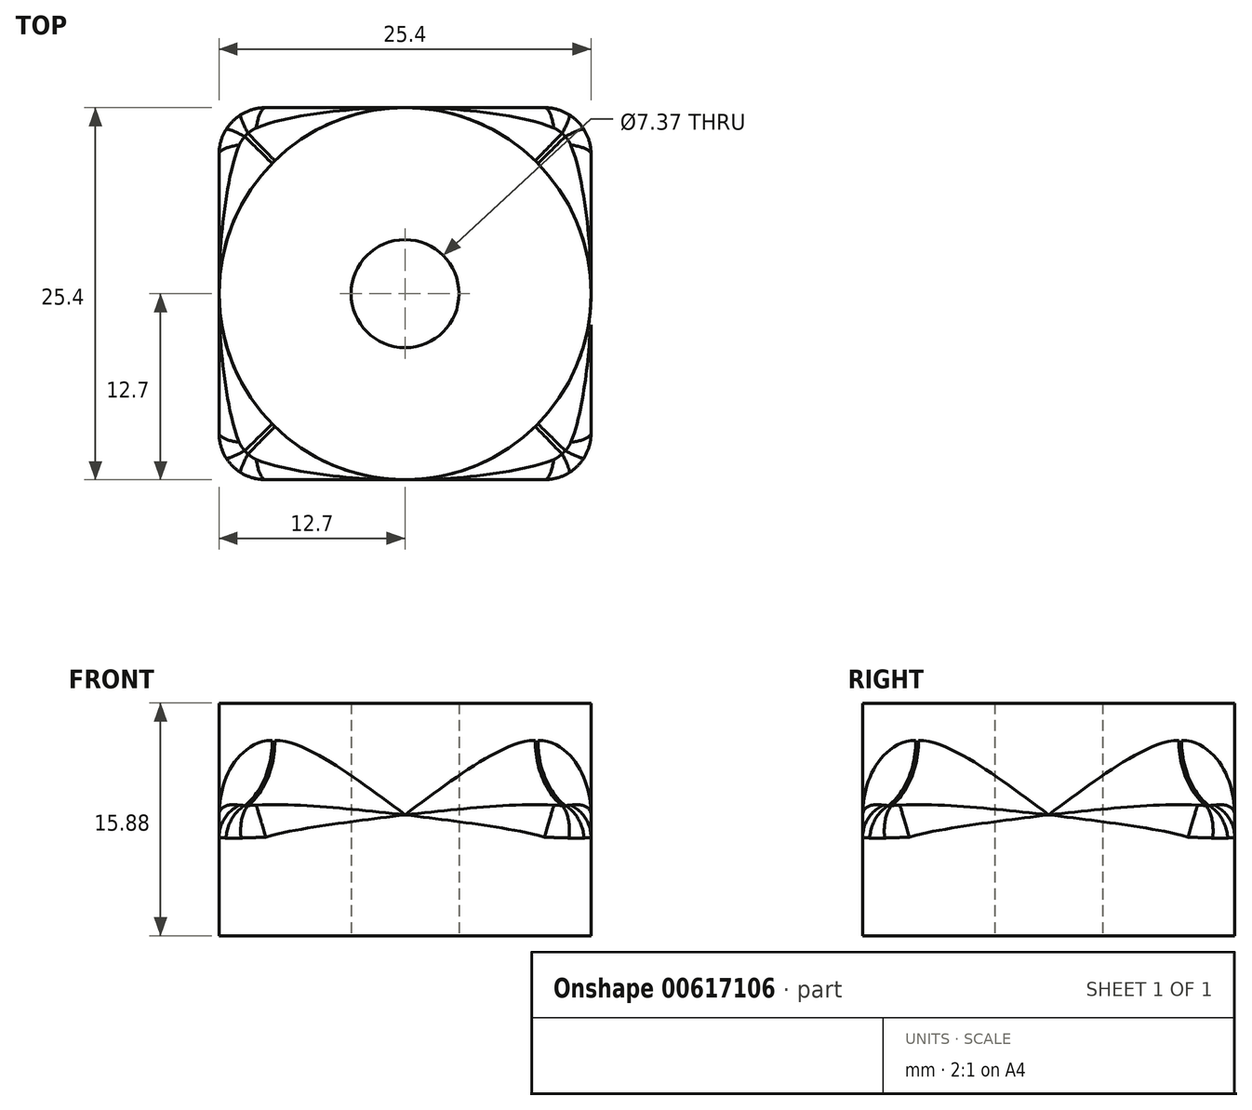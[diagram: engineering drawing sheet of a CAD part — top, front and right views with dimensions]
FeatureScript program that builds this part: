
annotation { "Feature Type Name" : "Feature", "Feature Type Description" : "" }
export const myFeature = defineFeature(function(context is Context, id is Id, definition is map)
    precondition{}
    {
        {
            var Q0;
            Q0=qCreatedBy(makeId("Top.planeOp"),FACE);
            var sketch = newSketch(context, id + "F0", { "sketchPlane" : qUnion([Q0])});
            skCircle(sketch, "E0", {"center": v(0, 0) * mm, "radius": 3.68 * mm});
            skCircle(sketch, "E1", {"center": v(0, 0) * mm, "radius": 12.7 * mm});
            skSolve(sketch);
        }
        {
            var Q0;
            Q0 = qSketchRegion(id + "F0", true);
            extrude(context, id + "F1", {"entities" : qUnion([Q0]), "depth" : 15.88 * mm, "offsetDistance" : 25.4 * mm});
        }
        {
            var Q0;
            Q0=qCreatedBy(makeId("Top.planeOp"),FACE);
            var sketch = newSketch(context, id + "F2", { "sketchPlane" : qUnion([Q0])});
            skLineSegment(sketch, "E2.bottom", {"start": v(12.7, -12.7) * mm, "end": v(-12.7, -12.7) * mm});
            skLineSegment(sketch, "E2.top", {"start": v(12.7, 12.7) * mm, "end": v(-12.7, 12.7) * mm});
            skLineSegment(sketch, "E2.left", {"start": v(12.7, -12.7) * mm, "end": v(12.7, 12.7) * mm});
            skLineSegment(sketch, "E2.right", {"start": v(-12.7, -12.7) * mm, "end": v(-12.7, 12.7) * mm});
            skCircle(sketch, "E3", {"center": v(0, 0) * mm, "radius": 3.68 * mm});
            skSolve(sketch);
        }
        {
            var Q0;
            Q0 = qSketchRegion(id + "F2", true);
            extrude(context, id + "F3", {"entities" : qUnion([Q0]), "operationType" : NewBodyOperationType.ADD, "depth" : 8.25 * mm, "offsetDistance" : 25.4 * mm});
        }
        {
            var Q0;
            Q0=makeQuery(id+"F3.boolean.opBoolean","INTERSECT",EDGE,{"disambiguationData":[OD(3.0)],"derivedFrom":[makeQuery(id+"F1.opExtrude","SWEPT_FACE",FACE,{"disambiguationData":[OSD([sQuery(id+"F0.wireOp",EDGE,"E1")])]}),makeQuery(id+"F3.opExtrude","CAP_FACE",FACE,{"disambiguationData":[OSD([sQuery(id+"F2.wireOp",EDGE,"E2.bottom"),sQuery(id+"F2.wireOp",EDGE,"E2.top"),sQuery(id+"F2.wireOp",EDGE,"E2.left"),sQuery(id+"F2.wireOp",EDGE,"E2.right")])],"isStart":false})]});
            fillet(context, id + "F4", {"entities" : qUnion([Q0]), "radius" : 5.08 * mm, "tangentPropagation" : true, "allowEdgeOverflow" : false});
        }
        {
            var Q0;
            Q0=makeQuery(id+"F3.opExtrude","SWEPT_EDGE",EDGE,{"disambiguationData":[OSD([sQuery(id+"F2.wireOp",EDGE,"E2.bottom"),sQuery(id+"F2.wireOp",EDGE,"E2.right")])]});
            var Q1;
            Q1=makeQuery(id+"F3.opExtrude","SWEPT_EDGE",EDGE,{"disambiguationData":[OSD([sQuery(id+"F2.wireOp",EDGE,"E2.bottom"),sQuery(id+"F2.wireOp",EDGE,"E2.left")])]});
            var Q2;
            Q2=makeQuery(id+"F3.opExtrude","SWEPT_EDGE",EDGE,{"disambiguationData":[OSD([sQuery(id+"F2.wireOp",EDGE,"E2.top"),sQuery(id+"F2.wireOp",EDGE,"E2.left")])]});
            var Q3;
            Q3=makeQuery(id+"F3.opExtrude","SWEPT_EDGE",EDGE,{"disambiguationData":[OSD([sQuery(id+"F2.wireOp",EDGE,"E2.top"),sQuery(id+"F2.wireOp",EDGE,"E2.right")])]});
            fillet(context, id + "F5", {"entities" : qUnion([Q0, Q1, Q2, Q3]), "radius" : 3.17 * mm, "tangentPropagation" : true, "allowEdgeOverflow" : false});
        }
        {
            var Q0;
            {var subQ0=sQuery(id+"F2.wireOp",EDGE,"E2.top");Q0=makeQuery(id+"F4.opFillet","BLEND_EDGE",EDGE,{"blendedFrom":[makeQuery(id+"F3.boolean.opBoolean","INTERSECT",EDGE,{"disambiguationData":[OD(3.0)],"derivedFrom":[makeQuery(id+"F1.opExtrude","SWEPT_FACE",FACE,{"disambiguationData":[OSD([sQuery(id+"F0.wireOp",EDGE,"E1")])]}),makeQuery(id+"F3.opExtrude","CAP_FACE",FACE,{"disambiguationData":[OSD([sQuery(id+"F2.wireOp",EDGE,"E2.bottom"),subQ0,sQuery(id+"F2.wireOp",EDGE,"E2.left"),sQuery(id+"F2.wireOp",EDGE,"E2.right"),sQuery(id+"F2.wireOp",EDGE,"E3")])],"isStart":false})]}),makeQuery(id+"F3.opExtrude","SWEPT_FACE",FACE,{"disambiguationData":[OSD([subQ0])]})],"blendedInto":[makeQuery(id+"F3.opExtrude","SWEPT_FACE",FACE,{"disambiguationData":[OSD([subQ0])]})]});}
            var Q1;
            {var subQ0=sQuery(id+"F2.wireOp",EDGE,"E2.top");Q1=makeQuery(id+"F4.opFillet","BLEND_EDGE",EDGE,{"blendedFrom":[makeQuery(id+"F3.boolean.opBoolean","INTERSECT",EDGE,{"disambiguationData":[OD(2.0)],"derivedFrom":[makeQuery(id+"F1.opExtrude","SWEPT_FACE",FACE,{"disambiguationData":[OSD([sQuery(id+"F0.wireOp",EDGE,"E1")])]}),makeQuery(id+"F3.opExtrude","CAP_FACE",FACE,{"disambiguationData":[OSD([sQuery(id+"F2.wireOp",EDGE,"E2.bottom"),subQ0,sQuery(id+"F2.wireOp",EDGE,"E2.left"),sQuery(id+"F2.wireOp",EDGE,"E2.right"),sQuery(id+"F2.wireOp",EDGE,"E3")])],"isStart":false})]}),makeQuery(id+"F3.opExtrude","SWEPT_FACE",FACE,{"disambiguationData":[OSD([subQ0])]})],"blendedInto":[makeQuery(id+"F3.opExtrude","SWEPT_FACE",FACE,{"disambiguationData":[OSD([subQ0])]})]});}
            var Q2;
            {var subQ0=sQuery(id+"F2.wireOp",EDGE,"E2.bottom");var subQ1=sQuery(id+"F2.wireOp",EDGE,"E2.left");var subQ2=makeQuery(id+"F3.opExtrude","CAP_FACE",FACE,{"disambiguationData":[OSD([subQ0,sQuery(id+"F2.wireOp",EDGE,"E2.top"),subQ1,sQuery(id+"F2.wireOp",EDGE,"E2.right"),sQuery(id+"F2.wireOp",EDGE,"E3")])],"isStart":false});Q2=makeQuery(id+"F5.opFillet","BLEND_EDGE",EDGE,{"blendedFrom":[makeQuery(id+"F3.opExtrude","SWEPT_EDGE",EDGE,{"disambiguationData":[OSD([subQ0,subQ1])]}),makeQuery(id+"F3.boolean.opBoolean","SPLIT",FACE,{"disambiguationData":[TD([makeQuery(id+"F1.opExtrude","SWEPT_FACE",FACE,{"disambiguationData":[OSD([sQuery(id+"F0.wireOp",EDGE,"E1")])]}),makeQuery(id+"F3.opExtrude","SWEPT_FACE",FACE,{"disambiguationData":[OSD([subQ0])]}),subQ2,makeQuery(id+"F3.opExtrude","SWEPT_FACE",FACE,{"disambiguationData":[OSD([subQ1])]})])],"derivedFrom":subQ2})],"blendedInto":[makeQuery(id+"F3.boolean.opBoolean","SPLIT",FACE,{"disambiguationData":[TD([makeQuery(id+"F1.opExtrude","SWEPT_FACE",FACE,{"disambiguationData":[OSD([sQuery(id+"F0.wireOp",EDGE,"E1")])]}),makeQuery(id+"F3.opExtrude","SWEPT_FACE",FACE,{"disambiguationData":[OSD([subQ0])]}),subQ2,makeQuery(id+"F3.opExtrude","SWEPT_FACE",FACE,{"disambiguationData":[OSD([subQ1])]})])],"derivedFrom":subQ2})]});}
            var Q3;
            {var subQ0=sQuery(id+"F2.wireOp",EDGE,"E2.bottom");var subQ1=sQuery(id+"F2.wireOp",EDGE,"E2.right");var subQ2=makeQuery(id+"F3.opExtrude","CAP_FACE",FACE,{"disambiguationData":[OSD([subQ0,sQuery(id+"F2.wireOp",EDGE,"E2.top"),sQuery(id+"F2.wireOp",EDGE,"E2.left"),subQ1,sQuery(id+"F2.wireOp",EDGE,"E3")])],"isStart":false});Q3=makeQuery(id+"F5.opFillet","BLEND_EDGE",EDGE,{"blendedFrom":[makeQuery(id+"F3.opExtrude","SWEPT_EDGE",EDGE,{"disambiguationData":[OSD([subQ0,subQ1])]}),makeQuery(id+"F3.boolean.opBoolean","SPLIT",FACE,{"disambiguationData":[TD([makeQuery(id+"F1.opExtrude","SWEPT_FACE",FACE,{"disambiguationData":[OSD([sQuery(id+"F0.wireOp",EDGE,"E1")])]}),makeQuery(id+"F3.opExtrude","SWEPT_FACE",FACE,{"disambiguationData":[OSD([subQ0])]}),subQ2,makeQuery(id+"F3.opExtrude","SWEPT_FACE",FACE,{"disambiguationData":[OSD([subQ1])]})])],"derivedFrom":subQ2})],"blendedInto":[makeQuery(id+"F3.boolean.opBoolean","SPLIT",FACE,{"disambiguationData":[TD([makeQuery(id+"F1.opExtrude","SWEPT_FACE",FACE,{"disambiguationData":[OSD([sQuery(id+"F0.wireOp",EDGE,"E1")])]}),makeQuery(id+"F3.opExtrude","SWEPT_FACE",FACE,{"disambiguationData":[OSD([subQ0])]}),subQ2,makeQuery(id+"F3.opExtrude","SWEPT_FACE",FACE,{"disambiguationData":[OSD([subQ1])]})])],"derivedFrom":subQ2})]});}
            var Q4;
            {var subQ0=sQuery(id+"F2.wireOp",EDGE,"E3");var subQ1=sQuery(id+"F2.wireOp",EDGE,"E2.right");var subQ2=sQuery(id+"F2.wireOp",EDGE,"E2.left");var subQ3=sQuery(id+"F2.wireOp",EDGE,"E2.top");var subQ4=sQuery(id+"F2.wireOp",EDGE,"E2.bottom");var subQ5=sQuery(id+"F0.wireOp",EDGE,"E1");Q4=makeQuery(id+"F5.opFillet","BLEND_EDGE",EDGE,{"blendedFrom":[makeQuery(id+"F3.opExtrude","SWEPT_EDGE",EDGE,{"disambiguationData":[OSD([subQ4,subQ2])]}),makeQuery(id+"F4.opFillet","BLEND_FACE",FACE,{"disambiguationData":[OSD([subQ5,subQ4,subQ3,subQ2,subQ1,subQ0]),TDD([makeQuery(id+"F3.boolean.opBoolean","INTERSECT",EDGE,{"disambiguationData":[OD(0.0)],"derivedFrom":[makeQuery(id+"F1.opExtrude","SWEPT_FACE",FACE,{"disambiguationData":[OSD([subQ5])]}),makeQuery(id+"F3.opExtrude","CAP_FACE",FACE,{"disambiguationData":[OSD([subQ4,subQ3,subQ2,subQ1,subQ0])],"isStart":false})]})]),OD(1.0)]})],"blendedInto":[makeQuery(id+"F4.opFillet","BLEND_FACE",FACE,{"disambiguationData":[OSD([subQ5,subQ4,subQ3,subQ2,subQ1,subQ0]),TDD([makeQuery(id+"F3.boolean.opBoolean","INTERSECT",EDGE,{"disambiguationData":[OD(0.0)],"derivedFrom":[makeQuery(id+"F1.opExtrude","SWEPT_FACE",FACE,{"disambiguationData":[OSD([subQ5])]}),makeQuery(id+"F3.opExtrude","CAP_FACE",FACE,{"disambiguationData":[OSD([subQ4,subQ3,subQ2,subQ1,subQ0])],"isStart":false})]})]),OD(1.0)]})]});}
            var Q5;
            {var subQ0=sQuery(id+"F2.wireOp",EDGE,"E3");var subQ1=sQuery(id+"F2.wireOp",EDGE,"E2.right");var subQ2=sQuery(id+"F2.wireOp",EDGE,"E2.left");var subQ3=sQuery(id+"F2.wireOp",EDGE,"E2.top");var subQ4=sQuery(id+"F2.wireOp",EDGE,"E2.bottom");var subQ5=sQuery(id+"F0.wireOp",EDGE,"E1");Q5=makeQuery(id+"F5.opFillet","BLEND_EDGE",EDGE,{"blendedFrom":[makeQuery(id+"F3.opExtrude","SWEPT_EDGE",EDGE,{"disambiguationData":[OSD([subQ4,subQ1])]}),makeQuery(id+"F4.opFillet","BLEND_FACE",FACE,{"disambiguationData":[OSD([subQ5,subQ4,subQ3,subQ2,subQ1,subQ0]),TDD([makeQuery(id+"F3.boolean.opBoolean","INTERSECT",EDGE,{"disambiguationData":[OD(1.0)],"derivedFrom":[makeQuery(id+"F1.opExtrude","SWEPT_FACE",FACE,{"disambiguationData":[OSD([subQ5])]}),makeQuery(id+"F3.opExtrude","CAP_FACE",FACE,{"disambiguationData":[OSD([subQ4,subQ3,subQ2,subQ1,subQ0])],"isStart":false})]})]),OD(0.0)]})],"blendedInto":[makeQuery(id+"F4.opFillet","BLEND_FACE",FACE,{"disambiguationData":[OSD([subQ5,subQ4,subQ3,subQ2,subQ1,subQ0]),TDD([makeQuery(id+"F3.boolean.opBoolean","INTERSECT",EDGE,{"disambiguationData":[OD(1.0)],"derivedFrom":[makeQuery(id+"F1.opExtrude","SWEPT_FACE",FACE,{"disambiguationData":[OSD([subQ5])]}),makeQuery(id+"F3.opExtrude","CAP_FACE",FACE,{"disambiguationData":[OSD([subQ4,subQ3,subQ2,subQ1,subQ0])],"isStart":false})]})]),OD(0.0)]})]});}
            fillet(context, id + "F6", {"entities" : qUnion([Q0, Q1, Q2, Q3, Q4, Q5]), "radius" : 2.54 * mm, "tangentPropagation" : true, "allowEdgeOverflow" : false});
        }
    });
